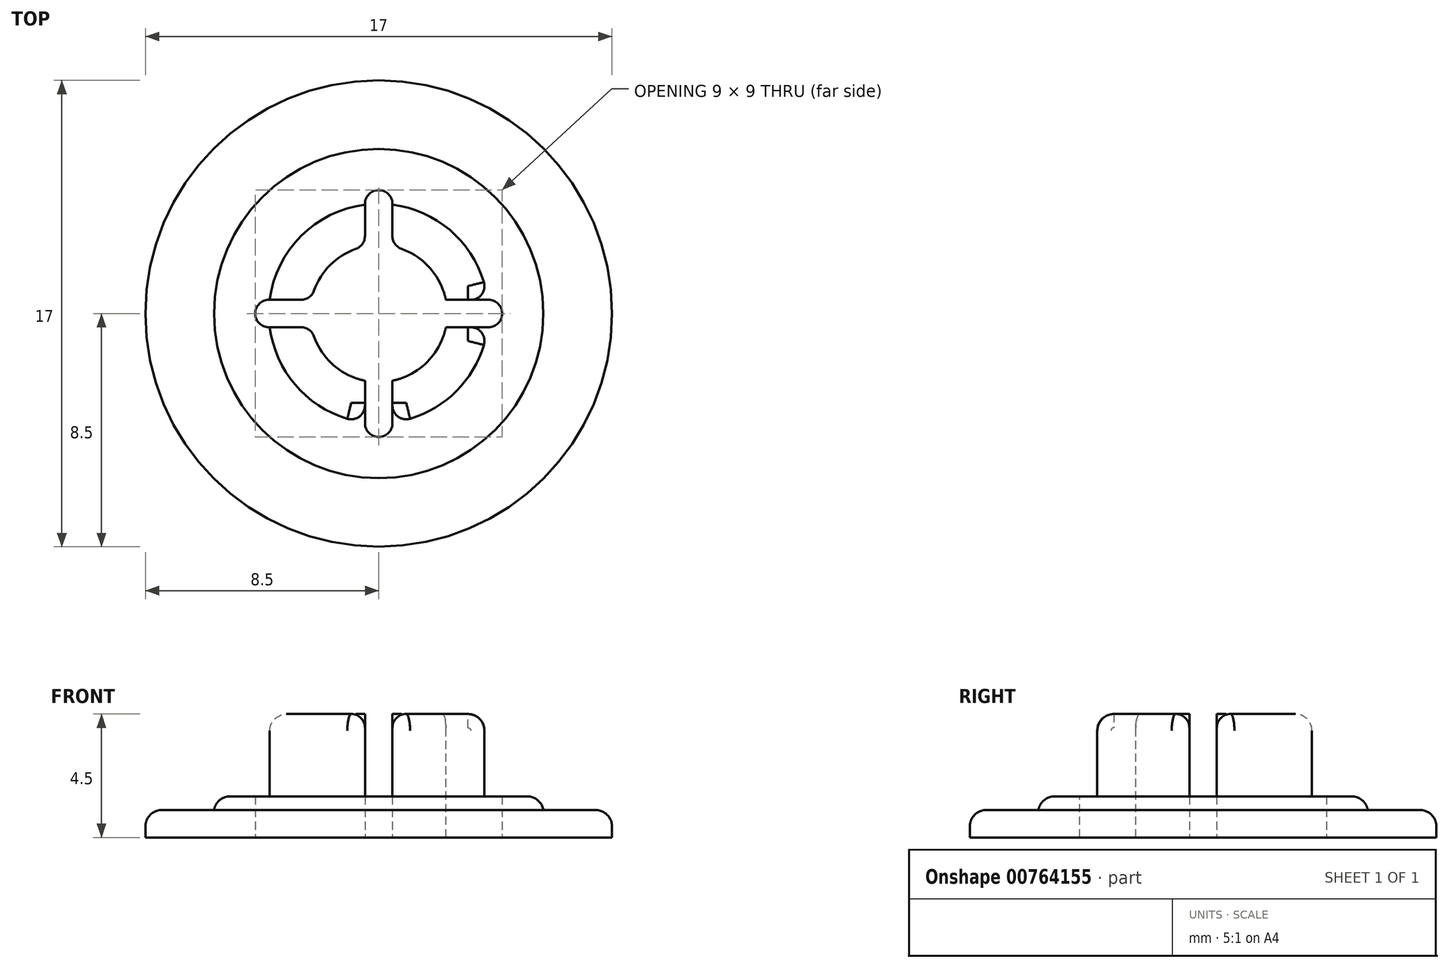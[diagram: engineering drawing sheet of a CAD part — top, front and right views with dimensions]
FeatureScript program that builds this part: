
annotation { "Feature Type Name" : "Feature", "Feature Type Description" : "" }
export const myFeature = defineFeature(function(context is Context, id is Id, definition is map)
    precondition{}
    {
        {
            var Q0;
            Q0=qCreatedBy(makeId("Top.planeOp"),FACE);
            var sketch = newSketch(context, id + "F0", { "sketchPlane" : qUnion([Q0])});
            skCircle(sketch, "E0", {"center": v(0, 0) * mm, "radius": 8.5 * mm});
            skSolve(sketch);
        }
        {
            var Q0;
            Q0 = qSketchRegion(id + "F0", true);
            extrude(context, id + "F1", {"entities" : qUnion([Q0]), "depth" : 1 * mm, "offsetDistance" : 25 * mm});
        }
        {
            var Q0;
            Q0=makeQuery(id+"F1.opExtrude","CAP_FACE",FACE,{"disambiguationData":[OSD([sQuery(id+"F0.wireOp",EDGE,"E0")])],"isStart":false});
            var sketch = newSketch(context, id + "F2", { "sketchPlane" : qUnion([Q0])});
            skCircle(sketch, "E1", {"center": v(0, 0) * mm, "radius": 6 * mm});
            skSolve(sketch);
        }
        {
            var Q0;
            Q0 = qSketchRegion(id + "F2", true);
            extrude(context, id + "F3", {"entities" : qUnion([Q0]), "operationType" : NewBodyOperationType.ADD, "depth" : .5 * mm, "offsetDistance" : 25 * mm});
        }
        {
            var Q0;
            Q0=makeQuery(id+"F3.opExtrude","CAP_FACE",FACE,{"disambiguationData":[OSD([sQuery(id+"F2.wireOp",EDGE,"E1")])],"isStart":false});
            var sketch = newSketch(context, id + "F4", { "sketchPlane" : qUnion([Q0])});
            skCircle(sketch, "E2", {"center": v(0, 0) * mm, "radius": 4 * mm});
            skSolve(sketch);
        }
        {
            var Q0;
            Q0 = qSketchRegion(id + "F4", true);
            extrude(context, id + "F5", {"entities" : qUnion([Q0]), "operationType" : NewBodyOperationType.ADD, "depth" : 3 * mm, "offsetDistance" : 25 * mm});
        }
        {
            var Q0;
            Q0=makeQuery(id+"F5.opExtrude","CAP_FACE",FACE,{"disambiguationData":[OSD([sQuery(id+"F4.wireOp",EDGE,"E2")])],"isStart":false});
            var sketch = newSketch(context, id + "F6", { "sketchPlane" : qUnion([Q0])});
            skCircle(sketch, "E3", {"center": v(0, 0) * mm, "radius": 2.5 * mm});
            skSolve(sketch);
        }
        {
            var Q0;
            Q0 = qSketchRegion(id + "F6", true);
            extrude(context, id + "F7", {"entities" : qUnion([Q0]), "operationType" : NewBodyOperationType.REMOVE, "oppositeDirection" : true, "depth" : 25 * mm, "offsetDistance" : 25 * mm});
        }
        {
            var Q0;
            Q0=makeQuery(id+"F5.opExtrude","CAP_EDGE",EDGE,{"disambiguationData":[OSD([sQuery(id+"F4.wireOp",EDGE,"E2")])],"isStart":false});
            var Q1;
            Q1=makeQuery(id+"F7.boolean.opBoolean","COPY",EDGE,{"derivedFrom":makeQuery(id+"F7.opExtrude","CAP_EDGE",EDGE,{"disambiguationData":[OSD([sQuery(id+"F6.wireOp",EDGE,"E3")])],"isStart":true})});
            var Q2;
            Q2=makeQuery(id+"F3.opExtrude","CAP_EDGE",EDGE,{"disambiguationData":[OSD([sQuery(id+"F2.wireOp",EDGE,"E1")])],"isStart":false});
            var Q3;
            Q3=makeQuery(id+"F1.opExtrude","CAP_EDGE",EDGE,{"disambiguationData":[OSD([sQuery(id+"F0.wireOp",EDGE,"E0")])],"isStart":false});
            fillet(context, id + "F8", {"entities" : qUnion([Q0, Q1, Q2, Q3]), "radius" : .6 * mm, "tangentPropagation" : true, "allowEdgeOverflow" : false});
        }
        {
            var Q0;
            Q0=qCreatedBy(makeId("Top.planeOp"),FACE);
            var sketch = newSketch(context, id + "F9", { "sketchPlane" : qUnion([Q0])});
            skLineSegment(sketch, "E4.bottom", {"start": v(4.5, -0.5) * mm, "end": v(-4.5, -0.5) * mm});
            skLineSegment(sketch, "E4.top", {"start": v(4.5, 0.5) * mm, "end": v(-4.5, 0.5) * mm});
            skLineSegment(sketch, "E4.left", {"start": v(4.5, -0.5) * mm, "end": v(4.5, 0.5) * mm});
            skLineSegment(sketch, "E4.right", {"start": v(-4.5, -0.5) * mm, "end": v(-4.5, 0.5) * mm});
            skPoint(sketch, "E4.middle", {"position": v(0, 0) * mm});
            skLineSegment(sketch, "E5.bottom", {"start": v(0.5, -4.5) * mm, "end": v(-0.5, -4.5) * mm});
            skLineSegment(sketch, "E5.top", {"start": v(0.5, 4.5) * mm, "end": v(-0.5, 4.5) * mm});
            skLineSegment(sketch, "E5.left", {"start": v(0.5, -4.5) * mm, "end": v(0.5, 4.5) * mm});
            skLineSegment(sketch, "E5.right", {"start": v(-0.5, -4.5) * mm, "end": v(-0.5, 4.5) * mm});
            skSolve(sketch);
        }
        {
            var Q0;
            Q0 = qSketchRegion(id + "F9", true);
            extrude(context, id + "F10", {"entities" : qUnion([Q0]), "operationType" : NewBodyOperationType.REMOVE, "depth" : 25 * mm, "offsetDistance" : 25 * mm});
        }
        {
            var Q0;
            {var subQ0=sQuery(id+"F9.wireOp",EDGE,"E5.left");Q0=makeQuery(id+"F10.boolean.opBoolean","INTERSECT",EDGE,{"derivedFrom":[makeQuery(id+"F5.opExtrude","SWEPT_FACE",FACE,{"disambiguationData":[OSD([sQuery(id+"F4.wireOp",EDGE,"E2")])]}),makeQuery(id+"F10.opExtrude","SWEPT_FACE",FACE,{"disambiguationData":[OSD([subQ0]),TDD([makeQuery(id+"F9.imprint","IMPRINT",EDGE,{"disambiguationData":[TD([[makeQuery(id+"F9.imprint","INTERSECT",VERTEX,{"derivedFrom":[sQuery(id+"F9.wireOp",EDGE,"E5.bottom"),subQ0]}),-1.0]])],"derivedFrom":subQ0})])]})]});}
            var Q1;
            {var subQ0=sQuery(id+"F9.wireOp",EDGE,"E5.right");Q1=makeQuery(id+"F10.boolean.opBoolean","INTERSECT",EDGE,{"derivedFrom":[makeQuery(id+"F5.opExtrude","SWEPT_FACE",FACE,{"disambiguationData":[OSD([sQuery(id+"F4.wireOp",EDGE,"E2")])]}),makeQuery(id+"F10.opExtrude","SWEPT_FACE",FACE,{"disambiguationData":[OSD([subQ0]),TDD([makeQuery(id+"F9.imprint","IMPRINT",EDGE,{"disambiguationData":[TD([[makeQuery(id+"F9.imprint","INTERSECT",VERTEX,{"derivedFrom":[sQuery(id+"F9.wireOp",EDGE,"E5.bottom"),subQ0]}),-1.0]])],"derivedFrom":subQ0})])]})]});}
            var Q2;
            {var subQ0=sQuery(id+"F9.wireOp",EDGE,"E4.bottom");Q2=makeQuery(id+"F10.boolean.opBoolean","INTERSECT",EDGE,{"derivedFrom":[makeQuery(id+"F5.opExtrude","SWEPT_FACE",FACE,{"disambiguationData":[OSD([sQuery(id+"F4.wireOp",EDGE,"E2")])]}),makeQuery(id+"F10.opExtrude","SWEPT_FACE",FACE,{"disambiguationData":[OSD([subQ0]),TDD([makeQuery(id+"F9.imprint","IMPRINT",EDGE,{"disambiguationData":[TD([[makeQuery(id+"F9.imprint","INTERSECT",VERTEX,{"derivedFrom":[subQ0,sQuery(id+"F9.wireOp",EDGE,"E4.left")]}),-1.0]])],"derivedFrom":subQ0})])]})]});}
            var Q3;
            {var subQ0=sQuery(id+"F9.wireOp",EDGE,"E4.top");Q3=makeQuery(id+"F10.boolean.opBoolean","INTERSECT",EDGE,{"derivedFrom":[makeQuery(id+"F5.opExtrude","SWEPT_FACE",FACE,{"disambiguationData":[OSD([sQuery(id+"F4.wireOp",EDGE,"E2")])]}),makeQuery(id+"F10.opExtrude","SWEPT_FACE",FACE,{"disambiguationData":[OSD([subQ0]),TDD([makeQuery(id+"F9.imprint","IMPRINT",EDGE,{"disambiguationData":[TD([[makeQuery(id+"F9.imprint","INTERSECT",VERTEX,{"derivedFrom":[subQ0,sQuery(id+"F9.wireOp",EDGE,"E4.left")]}),-1.0]])],"derivedFrom":subQ0})])]})]});}
            var Q4;
            {var subQ0=sQuery(id+"F9.wireOp",EDGE,"E4.top");Q4=makeQuery(id+"F10.boolean.opBoolean","INTERSECT",EDGE,{"derivedFrom":[makeQuery(id+"F7.boolean.opBoolean","COPY",FACE,{"derivedFrom":makeQuery(id+"F7.opExtrude","SWEPT_FACE",FACE,{"disambiguationData":[OSD([sQuery(id+"F6.wireOp",EDGE,"E3")])]})}),makeQuery(id+"F10.opExtrude","SWEPT_FACE",FACE,{"disambiguationData":[OSD([subQ0]),TDD([makeQuery(id+"F9.imprint","IMPRINT",EDGE,{"disambiguationData":[TD([[makeQuery(id+"F9.imprint","INTERSECT",VERTEX,{"derivedFrom":[subQ0,sQuery(id+"F9.wireOp",EDGE,"E4.right")]}),1.0]])],"derivedFrom":subQ0})])]})]});}
            var Q5;
            {var subQ0=sQuery(id+"F9.wireOp",EDGE,"E5.right");Q5=makeQuery(id+"F10.boolean.opBoolean","INTERSECT",EDGE,{"derivedFrom":[makeQuery(id+"F7.boolean.opBoolean","COPY",FACE,{"derivedFrom":makeQuery(id+"F7.opExtrude","SWEPT_FACE",FACE,{"disambiguationData":[OSD([sQuery(id+"F6.wireOp",EDGE,"E3")])]})}),makeQuery(id+"F10.opExtrude","SWEPT_FACE",FACE,{"disambiguationData":[OSD([subQ0]),TDD([makeQuery(id+"F9.imprint","IMPRINT",EDGE,{"disambiguationData":[TD([[makeQuery(id+"F9.imprint","INTERSECT",VERTEX,{"derivedFrom":[sQuery(id+"F9.wireOp",EDGE,"E5.top"),subQ0]}),1.0]])],"derivedFrom":subQ0})])]})]});}
            var Q6;
            {var subQ0=sQuery(id+"F9.wireOp",EDGE,"E4.bottom");Q6=makeQuery(id+"F10.boolean.opBoolean","INTERSECT",EDGE,{"derivedFrom":[makeQuery(id+"F7.boolean.opBoolean","COPY",FACE,{"derivedFrom":makeQuery(id+"F7.opExtrude","SWEPT_FACE",FACE,{"disambiguationData":[OSD([sQuery(id+"F6.wireOp",EDGE,"E3")])]})}),makeQuery(id+"F10.opExtrude","SWEPT_FACE",FACE,{"disambiguationData":[OSD([subQ0]),TDD([makeQuery(id+"F9.imprint","IMPRINT",EDGE,{"disambiguationData":[TD([[makeQuery(id+"F9.imprint","INTERSECT",VERTEX,{"derivedFrom":[subQ0,sQuery(id+"F9.wireOp",EDGE,"E4.right")]}),1.0]])],"derivedFrom":subQ0})])]})]});}
            var Q7;
            {var subQ0=sQuery(id+"F9.wireOp",EDGE,"E5.left");Q7=makeQuery(id+"F10.boolean.opBoolean","INTERSECT",EDGE,{"derivedFrom":[makeQuery(id+"F7.boolean.opBoolean","COPY",FACE,{"derivedFrom":makeQuery(id+"F7.opExtrude","SWEPT_FACE",FACE,{"disambiguationData":[OSD([sQuery(id+"F6.wireOp",EDGE,"E3")])]})}),makeQuery(id+"F10.opExtrude","SWEPT_FACE",FACE,{"disambiguationData":[OSD([subQ0]),TDD([makeQuery(id+"F9.imprint","IMPRINT",EDGE,{"disambiguationData":[TD([[makeQuery(id+"F9.imprint","INTERSECT",VERTEX,{"derivedFrom":[sQuery(id+"F9.wireOp",EDGE,"E5.top"),subQ0]}),1.0]])],"derivedFrom":subQ0})])]})]});}
            var Q8;
            Q8=makeQuery(id+"F10.boolean.opBoolean","COPY",EDGE,{"derivedFrom":makeQuery(id+"F10.opExtrude","SWEPT_EDGE",EDGE,{"disambiguationData":[OSD([sQuery(id+"F9.wireOp",EDGE,"E5.top"),sQuery(id+"F9.wireOp",EDGE,"E5.right")])]})});
            var Q9;
            Q9=makeQuery(id+"F10.boolean.opBoolean","COPY",EDGE,{"derivedFrom":makeQuery(id+"F10.opExtrude","SWEPT_EDGE",EDGE,{"disambiguationData":[OSD([sQuery(id+"F9.wireOp",EDGE,"E5.top"),sQuery(id+"F9.wireOp",EDGE,"E5.left")])]})});
            var Q10;
            Q10=makeQuery(id+"F10.boolean.opBoolean","COPY",EDGE,{"derivedFrom":makeQuery(id+"F10.opExtrude","SWEPT_EDGE",EDGE,{"disambiguationData":[OSD([sQuery(id+"F9.wireOp",EDGE,"E4.top"),sQuery(id+"F9.wireOp",EDGE,"E4.right")])]})});
            var Q11;
            Q11=makeQuery(id+"F10.boolean.opBoolean","COPY",EDGE,{"derivedFrom":makeQuery(id+"F10.opExtrude","SWEPT_EDGE",EDGE,{"disambiguationData":[OSD([sQuery(id+"F9.wireOp",EDGE,"E4.bottom"),sQuery(id+"F9.wireOp",EDGE,"E4.right")])]})});
            var Q12;
            Q12=makeQuery(id+"F10.boolean.opBoolean","COPY",EDGE,{"derivedFrom":makeQuery(id+"F10.opExtrude","SWEPT_EDGE",EDGE,{"disambiguationData":[OSD([sQuery(id+"F9.wireOp",EDGE,"E5.bottom"),sQuery(id+"F9.wireOp",EDGE,"E5.right")])]})});
            var Q13;
            Q13=makeQuery(id+"F10.boolean.opBoolean","COPY",EDGE,{"derivedFrom":makeQuery(id+"F10.opExtrude","SWEPT_EDGE",EDGE,{"disambiguationData":[OSD([sQuery(id+"F9.wireOp",EDGE,"E5.bottom"),sQuery(id+"F9.wireOp",EDGE,"E5.left")])]})});
            var Q14;
            Q14=makeQuery(id+"F10.boolean.opBoolean","COPY",EDGE,{"derivedFrom":makeQuery(id+"F10.opExtrude","SWEPT_EDGE",EDGE,{"disambiguationData":[OSD([sQuery(id+"F9.wireOp",EDGE,"E4.bottom"),sQuery(id+"F9.wireOp",EDGE,"E4.left")])]})});
            var Q15;
            Q15=makeQuery(id+"F10.boolean.opBoolean","COPY",EDGE,{"derivedFrom":makeQuery(id+"F10.opExtrude","SWEPT_EDGE",EDGE,{"disambiguationData":[OSD([sQuery(id+"F9.wireOp",EDGE,"E4.top"),sQuery(id+"F9.wireOp",EDGE,"E4.left")])]})});
            fillet(context, id + "F11", {"entities" : qUnion([Q0, Q1, Q2, Q3, Q4, Q5, Q6, Q7, Q8, Q9, Q10, Q11, Q12, Q13, Q14, Q15]), "radius" : .5 * mm, "tangentPropagation" : true, "allowEdgeOverflow" : false});
        }
    });
